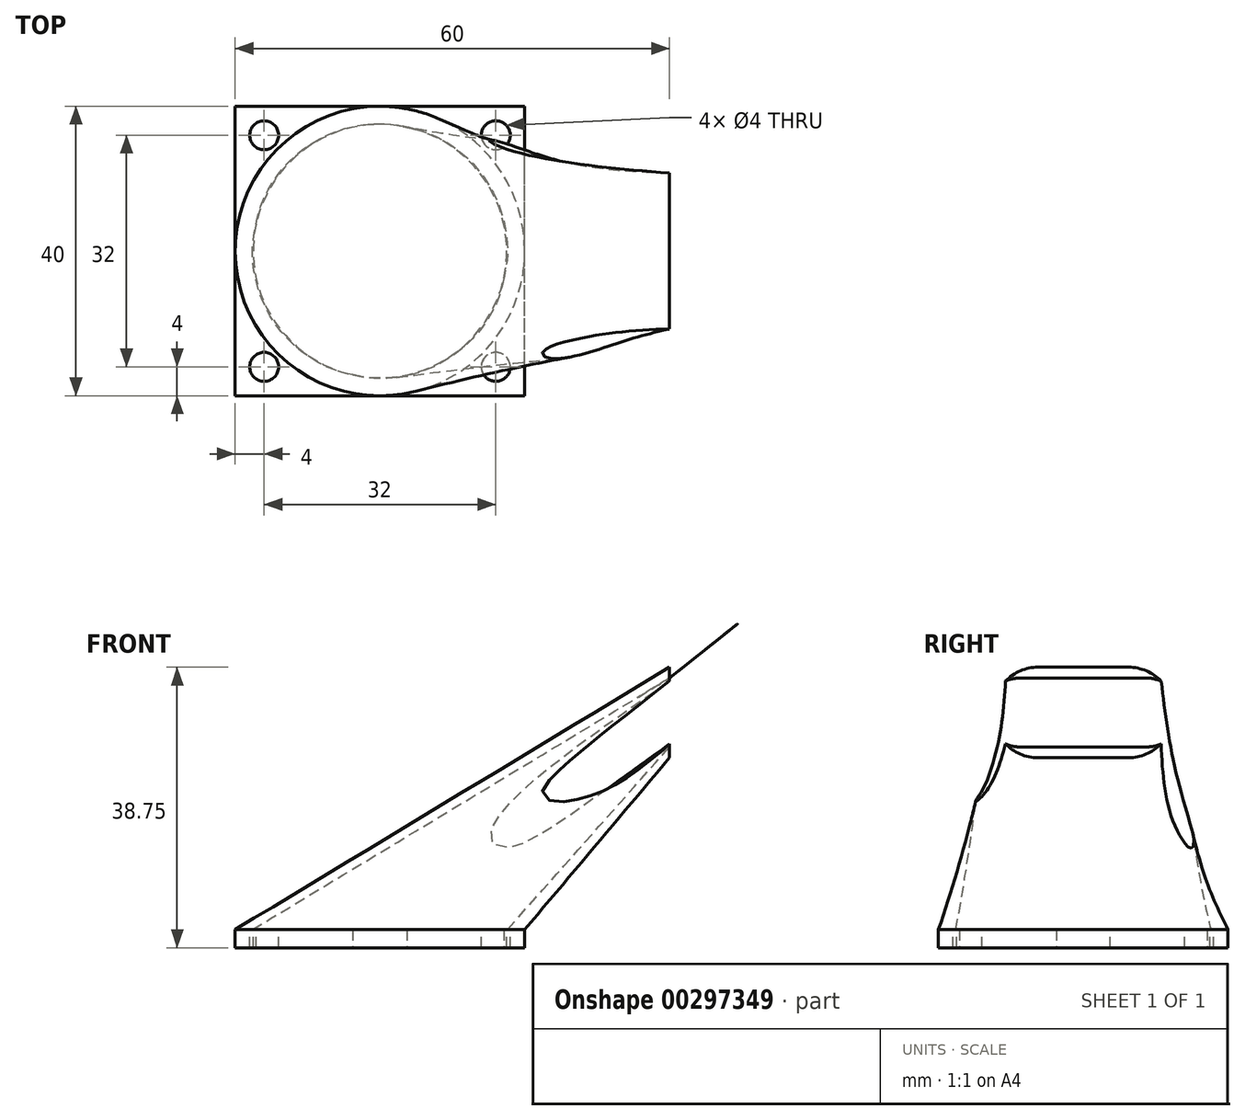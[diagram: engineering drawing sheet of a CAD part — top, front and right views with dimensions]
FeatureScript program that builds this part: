
annotation { "Feature Type Name" : "Feature", "Feature Type Description" : "" }
export const myFeature = defineFeature(function(context is Context, id is Id, definition is map)
    precondition{}
    {
        {
            var Q0;
            Q0=qCreatedBy(makeId("Front.planeOp"),FACE);
            var sketch = newSketch(context, id + "F0", { "sketchPlane" : qUnion([Q0])});
            skArc(sketch, "E0", {"start": v(40, 30) * mm, "mid": v(15.98, 20.36) * mm, "end": v(0, 0) * mm});
            skSolve(sketch);
        }
        {
            var Q0;
            Q0=qCreatedBy(makeId("Top.planeOp"),FACE);
            var sketch = newSketch(context, id + "F1", { "sketchPlane" : qUnion([Q0])});
            skCircle(sketch, "E1", {"center": v(0, 0) * mm, "radius": 17.5 * mm, "construction": true});
            skCircle(sketch, "E2", {"center": v(0, 0) * mm, "radius": 20 * mm});
            skSolve(sketch);
        }
        {
            var Q0;
            Q0=qCreatedBy(makeId("Right.planeOp"),FACE);
            cPlane(context, id + "F2", {"entities" : qUnion([Q0]), "cplaneType" : CPlaneType.OFFSET, "offset" : 40 * mm, "width" : 150 * mm, "height" : 150 * mm});
        }
        {
            var Q0;
            Q0=qCreatedBy(id+"F2.planeOp",FACE);
            var sketch = newSketch(context, id + "F3", { "sketchPlane" : qUnion([Q0])});
            skLineSegment(sketch, "E3.bottom", {"start": v(-6.25, 33.75) * mm, "end": v(6.25, 33.75) * mm, "construction": true});
            skLineSegment(sketch, "E3.top", {"start": v(-6.25, 26.25) * mm, "end": v(6.25, 26.25) * mm, "construction": true});
            skArc(sketch, "E4", {"start": v(-6.25, 33.75) * mm, "mid": v(-10, 30) * mm, "end": v(-6.25, 26.25) * mm, "construction": true});
            skArc(sketch, "E5", {"start": v(6.25, 26.25) * mm, "mid": v(10, 30) * mm, "end": v(6.25, 33.75) * mm, "construction": true});
            skLineSegment(sketch, "E6", {"start": v(-6.25, 30) * mm, "end": v(6.25, 30) * mm, "construction": true});
            skLineSegment(sketch, "E7", {"start": v(0, 33.75) * mm, "end": v(0, 26.25) * mm, "construction": true});
            skPoint(sketch, "E8", {"position": v(0, 30) * mm});
            skLineSegment(sketch, "E9.0", {"start": v(-6.25, 36.25) * mm, "end": v(6.25, 36.25) * mm});
            skArc(sketch, "E9.1", {"start": v(-6.25, 36.25) * mm, "mid": v(-12.5, 30) * mm, "end": v(-6.25, 23.75) * mm});
            skLineSegment(sketch, "E9.2", {"start": v(-6.25, 23.75) * mm, "end": v(6.25, 23.75) * mm});
            skArc(sketch, "E9.3", {"start": v(6.25, 23.75) * mm, "mid": v(12.5, 30) * mm, "end": v(6.25, 36.25) * mm});
            skSolve(sketch);
        }
        {
            var Q0;
            Q0=makeQuery(id+"F1.imprint","IMPRINT",FACE,{"disambiguationData":[TD([[makeQuery(id+"F1.imprint","IMPRINT",EDGE,{"derivedFrom":sQuery(id+"F1.wireOp",EDGE,"E2")}),1.0]])]});
            var Q1;
            Q1=makeQuery(id+"F3.imprint","IMPRINT",FACE,{"disambiguationData":[TD([[makeQuery(id+"F3.imprint","IMPRINT",EDGE,{"derivedFrom":sQuery(id+"F3.wireOp",EDGE,"E9.0")}),-1.0]])]});
            loft(context, id + "F4", {"sheetProfilesArray" : [{ "sheetProfileEntities" : qUnion([Q0]) }, { "sheetProfileEntities" : qUnion([Q1]) }]});
        }
        {
            var Q0;
            Q0=makeQuery(id+"F4.opLoft","CAP_FACE",FACE,{"disambiguationData":[OSD([makeQuery(id+"F3.imprint","IMPRINT",FACE,{"disambiguationData":[TD([[makeQuery(id+"F3.imprint","IMPRINT",EDGE,{"derivedFrom":sQuery(id+"F3.wireOp",EDGE,"E9.0")}),-1.0]])]})])],"isStart":true});
            var sketch = newSketch(context, id + "F5", { "sketchPlane" : qUnion([Q0])});
            skFitSpline(sketch, "E10.0", {"points": [v(-8.75, 25.25) * mm, v(-2.92, 25.25) * mm, v(2.92, 25.25) * mm, v(8.75, 25.25) * mm]});
            skFitSpline(sketch, "E10.1", {"points": [v(-8.75, 34.75) * mm, v(-8.9, 34.75) * mm, v(-9.22, 34.73) * mm, v(-9.83, 34.64) * mm, v(-10.58, 34.42) * mm, v(-11.4, 33.97) * mm, v(-12.37, 33.18) * mm, v(-13.25, 31.87) * mm, v(-13.62, 30) * mm, v(-13.25, 28.13) * mm, v(-12.37, 26.82) * mm, v(-11.53, 26.12) * mm, v(-11, 25.8) * mm, v(-10.57, 25.6) * mm, v(-10.13, 25.45) * mm, v(-9.53, 25.3) * mm, v(-9.06, 25.25) * mm, v(-8.75, 25.25) * mm]});
            skFitSpline(sketch, "E10.2", {"points": [v(8.75, 34.75) * mm, v(2.92, 34.75) * mm, v(-2.92, 34.75) * mm, v(-8.75, 34.75) * mm]});
            skFitSpline(sketch, "E10.3", {"points": [v(8.75, 25.25) * mm, v(8.9, 25.25) * mm, v(9.22, 25.27) * mm, v(9.83, 25.36) * mm, v(10.58, 25.58) * mm, v(11.4, 26.03) * mm, v(12.37, 26.82) * mm, v(13.25, 28.13) * mm, v(13.62, 30) * mm, v(13.25, 31.87) * mm, v(12.37, 33.18) * mm, v(11.53, 33.88) * mm, v(11, 34.2) * mm, v(10.57, 34.4) * mm, v(10.13, 34.55) * mm, v(9.53, 34.7) * mm, v(9.06, 34.75) * mm, v(8.75, 34.75) * mm]});
            skSolve(sketch);
        }
        {
            var Q0;
            Q0=makeQuery(id+"F4.opLoft","CAP_FACE",FACE,{"disambiguationData":[OSD([makeQuery(id+"F1.imprint","IMPRINT",FACE,{"disambiguationData":[TD([[makeQuery(id+"F1.imprint","IMPRINT",EDGE,{"derivedFrom":sQuery(id+"F1.wireOp",EDGE,"E2")}),1.0]])]})])],"isStart":true});
            var sketch = newSketch(context, id + "F6", { "sketchPlane" : qUnion([Q0])});
            skFitSpline(sketch, "E11.0", {"points": [v(3.74, -17.1) * mm, v(4.86, -16.85) * mm, v(7.05, -16.14) * mm, v(10.06, -14.46) * mm, v(12.69, -12.22) * mm, v(14.83, -9.5) * mm, v(16.4, -6.43) * mm, v(17.34, -3.1) * mm, v(17.6, 0.34) * mm, v(17.34, 2.62) * mm, v(17.1, 3.74) * mm]});
            skFitSpline(sketch, "E11.1", {"points": [v(-17.1, -3.74) * mm, v(-16.85, -4.86) * mm, v(-16.14, -7.05) * mm, v(-14.46, -10.06) * mm, v(-12.22, -12.69) * mm, v(-9.5, -14.83) * mm, v(-6.43, -16.4) * mm, v(-3.1, -17.34) * mm, v(0.34, -17.6) * mm, v(2.62, -17.34) * mm, v(3.74, -17.1) * mm]});
            skFitSpline(sketch, "E11.2", {"points": [v(-3.74, 17.1) * mm, v(-4.86, 16.85) * mm, v(-7.05, 16.14) * mm, v(-10.06, 14.46) * mm, v(-12.69, 12.22) * mm, v(-14.83, 9.5) * mm, v(-16.4, 6.43) * mm, v(-17.34, 3.1) * mm, v(-17.6, -0.34) * mm, v(-17.34, -2.62) * mm, v(-17.1, -3.74) * mm]});
            skFitSpline(sketch, "E11.3", {"points": [v(17.1, 3.74) * mm, v(16.85, 4.86) * mm, v(16.14, 7.05) * mm, v(14.46, 10.06) * mm, v(12.22, 12.69) * mm, v(9.5, 14.83) * mm, v(6.43, 16.4) * mm, v(3.1, 17.34) * mm, v(-0.34, 17.6) * mm, v(-2.62, 17.34) * mm, v(-3.74, 17.1) * mm]});
            skSolve(sketch);
        }
        {
            var Q0;
            Q0 = qSketchRegion(id + "F6", true);
            var Q1;
            Q1 = qSketchRegion(id + "F5", true);
            loft(context, id + "F7", {"operationType" : NewBodyOperationType.REMOVE, "sheetProfilesArray" : [{ "sheetProfileEntities" : qUnion([Q0]) }, { "sheetProfileEntities" : qUnion([Q1]) }]});
        }
        {
            var Q0;
            Q0=makeQuery(id+"F4.opLoft","CAP_FACE",FACE,{"disambiguationData":[OSD([makeQuery(id+"F1.imprint","IMPRINT",FACE,{"disambiguationData":[TD([[makeQuery(id+"F1.imprint","IMPRINT",EDGE,{"derivedFrom":sQuery(id+"F1.wireOp",EDGE,"E2")}),1.0]])]})])],"isStart":true});
            var sketch = newSketch(context, id + "F8", { "sketchPlane" : qUnion([Q0])});
            skLineSegment(sketch, "E12.bottom", {"start": v(20, 20) * mm, "end": v(-20, 20) * mm});
            skLineSegment(sketch, "E12.top", {"start": v(20, -20) * mm, "end": v(-20, -20) * mm});
            skLineSegment(sketch, "E12.left", {"start": v(20, 20) * mm, "end": v(20, -20) * mm});
            skLineSegment(sketch, "E12.right", {"start": v(-20, 20) * mm, "end": v(-20, -20) * mm});
            skPoint(sketch, "E12.middle", {"position": v(0, 0) * mm});
            skCircle(sketch, "E13", {"center": v(-16, 16) * mm, "radius": 2 * mm});
            skLineSegment(sketch, "E14", {"start": v(0, 0) * mm, "end": v(0, 20) * mm, "construction": true});
            skLineSegment(sketch, "E15", {"start": v(0, 0) * mm, "end": v(20, 0) * mm, "construction": true});
            skCircle(sketch, "E16.MirrorC", {"center": v(16, 16) * mm, "radius": 2 * mm});
            skCircle(sketch, "E17.MirrorC", {"center": v(16, -16) * mm, "radius": 2 * mm});
            skCircle(sketch, "E18.MirrorC", {"center": v(-16, -16) * mm, "radius": 2 * mm});
            skFitSpline(sketch, "E19.0", {"points": [v(-17.1, -3.74) * mm, v(-17.34, -2.62) * mm, v(-17.48, -1.48) * mm, v(-17.5, -0.33) * mm, v(-17.5, 0.24) * mm, v(-17.5, 0.81) * mm, v(-17.45, 1.38) * mm, v(-17.4, 1.96) * mm, v(-17.33, 2.52) * mm, v(-17.23, 3.09) * mm, v(-17.12, 3.65) * mm, v(-17, 4.2) * mm, v(-16.84, 4.76) * mm, v(-16.68, 5.31) * mm, v(-16.5, 5.86) * mm, v(-16.3, 6.39) * mm, v(-16.08, 6.92) * mm, v(-15.85, 7.44) * mm, v(-15.59, 7.95) * mm, v(-15.33, 8.47) * mm, v(-15.04, 8.96) * mm, v(-14.73, 9.44) * mm, v(-14.42, 9.93) * mm, v(-14.1, 10.4) * mm, v(-13.74, 10.84) * mm, v(-13.38, 11.3) * mm, v(-13, 11.72) * mm, v(-12.6, 12.14) * mm, v(-12.2, 12.55) * mm, v(-11.8, 12.94) * mm, v(-11.36, 13.31) * mm, v(-10.92, 13.69) * mm, v(-10.47, 14.04) * mm, v(-10, 14.36) * mm, v(-9.53, 14.7) * mm, v(-9.04, 15) * mm, v(-8.54, 15.27) * mm, v(-8.04, 15.55) * mm, v(-7.53, 15.8) * mm, v(-7, 16.04) * mm, v(-5.95, 16.5) * mm, v(-4.86, 16.85) * mm, v(-3.74, 17.1) * mm]});
            skFitSpline(sketch, "E20.0", {"points": [v(-3.74, 17.1) * mm, v(-2.62, 17.34) * mm, v(-1.48, 17.48) * mm, v(-0.33, 17.5) * mm, v(0.24, 17.5) * mm, v(0.81, 17.5) * mm, v(1.38, 17.45) * mm, v(1.96, 17.4) * mm, v(2.52, 17.33) * mm, v(3.09, 17.23) * mm, v(3.65, 17.12) * mm, v(4.2, 17) * mm, v(4.76, 16.84) * mm, v(5.31, 16.68) * mm, v(5.86, 16.5) * mm, v(6.39, 16.3) * mm, v(6.92, 16.08) * mm, v(7.44, 15.85) * mm, v(7.95, 15.59) * mm, v(8.47, 15.33) * mm, v(8.96, 15.04) * mm, v(9.44, 14.73) * mm, v(9.93, 14.42) * mm, v(10.4, 14.1) * mm, v(10.84, 13.74) * mm, v(11.3, 13.38) * mm, v(11.72, 13) * mm, v(12.14, 12.6) * mm, v(12.55, 12.2) * mm, v(12.94, 11.8) * mm, v(13.31, 11.36) * mm, v(13.69, 10.92) * mm, v(14.04, 10.47) * mm, v(14.36, 10) * mm, v(14.7, 9.53) * mm, v(15, 9.04) * mm, v(15.27, 8.54) * mm, v(15.55, 8.04) * mm, v(15.8, 7.53) * mm, v(16.04, 7) * mm, v(16.5, 5.95) * mm, v(16.85, 4.86) * mm, v(17.1, 3.74) * mm]});
            skFitSpline(sketch, "E21.0", {"points": [v(17.1, 3.74) * mm, v(17.34, 2.62) * mm, v(17.48, 1.48) * mm, v(17.5, 0.33) * mm, v(17.5, -0.24) * mm, v(17.5, -0.81) * mm, v(17.45, -1.38) * mm, v(17.4, -1.96) * mm, v(17.33, -2.52) * mm, v(17.23, -3.09) * mm, v(17.12, -3.65) * mm, v(17, -4.2) * mm, v(16.84, -4.76) * mm, v(16.68, -5.31) * mm, v(16.5, -5.86) * mm, v(16.3, -6.39) * mm, v(16.08, -6.92) * mm, v(15.85, -7.44) * mm, v(15.59, -7.95) * mm, v(15.33, -8.47) * mm, v(15.04, -8.96) * mm, v(14.73, -9.44) * mm, v(14.42, -9.93) * mm, v(14.1, -10.4) * mm, v(13.74, -10.84) * mm, v(13.38, -11.3) * mm, v(13, -11.72) * mm, v(12.6, -12.14) * mm, v(12.2, -12.55) * mm, v(11.8, -12.94) * mm, v(11.36, -13.31) * mm, v(10.92, -13.69) * mm, v(10.47, -14.04) * mm, v(10, -14.36) * mm, v(9.53, -14.7) * mm, v(9.04, -15) * mm, v(8.54, -15.27) * mm, v(8.04, -15.55) * mm, v(7.53, -15.8) * mm, v(7, -16.04) * mm, v(5.95, -16.5) * mm, v(4.86, -16.85) * mm, v(3.74, -17.1) * mm]});
            skFitSpline(sketch, "E22.0", {"points": [v(3.74, -17.1) * mm, v(2.62, -17.34) * mm, v(1.48, -17.48) * mm, v(0.33, -17.5) * mm, v(-0.24, -17.5) * mm, v(-0.81, -17.5) * mm, v(-1.38, -17.45) * mm, v(-1.96, -17.4) * mm, v(-2.52, -17.33) * mm, v(-3.09, -17.23) * mm, v(-3.65, -17.12) * mm, v(-4.2, -17) * mm, v(-4.76, -16.84) * mm, v(-5.31, -16.68) * mm, v(-5.86, -16.5) * mm, v(-6.39, -16.3) * mm, v(-6.92, -16.08) * mm, v(-7.44, -15.85) * mm, v(-7.95, -15.59) * mm, v(-8.47, -15.33) * mm, v(-8.96, -15.04) * mm, v(-9.44, -14.73) * mm, v(-9.93, -14.42) * mm, v(-10.4, -14.1) * mm, v(-10.84, -13.74) * mm, v(-11.3, -13.38) * mm, v(-11.72, -13) * mm, v(-12.14, -12.6) * mm, v(-12.55, -12.2) * mm, v(-12.94, -11.8) * mm, v(-13.31, -11.36) * mm, v(-13.69, -10.92) * mm, v(-14.04, -10.47) * mm, v(-14.36, -10) * mm, v(-14.7, -9.53) * mm, v(-15, -9.04) * mm, v(-15.27, -8.54) * mm, v(-15.55, -8.04) * mm, v(-15.8, -7.53) * mm, v(-16.04, -7) * mm, v(-16.5, -5.95) * mm, v(-16.85, -4.86) * mm, v(-17.1, -3.74) * mm]});
            skSolve(sketch);
        }
        {
            var Q0;
            Q0 = qSketchRegion(id + "F8", true);
            extrude(context, id + "F9", {"entities" : qUnion([Q0]), "operationType" : NewBodyOperationType.ADD, "depth" : 2.5 * mm});
        }
    });
